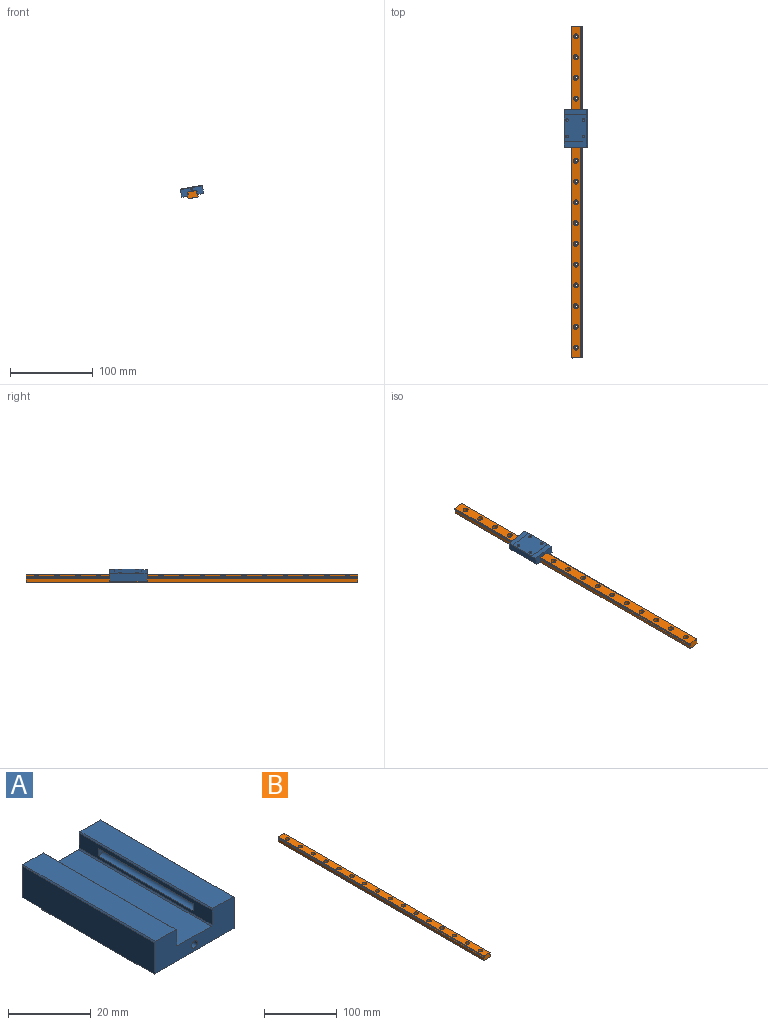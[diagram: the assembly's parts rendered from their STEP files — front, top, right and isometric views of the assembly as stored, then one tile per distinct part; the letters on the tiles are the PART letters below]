
ASSEMBLY  parts=2 mates=1
PART A: 37 faces, bbox 27x45.4x10 mm
  f0: plane 45.4x0.3mm, normal (-0.71,0,0.71), area 19.3mm2, adj f3,f6,f22,f23
  f1: plane 45.4x0.3mm, normal (0.71,0,0.71), area 19.3mm2, adj f10,f11,f22,f23
  f2: plane 45.4x0.3mm, normal (0.71,0,0.71), area 19.3mm2, adj f6,f7,f22,f23
  f3: plane 45.4x4.4mm, normal (-1,0,0), area 129.2mm2, adj f0,f5,f17,f20,f22,f23,f24
  f4: plane 45.4x11.4mm, normal (0,0,1), area 517.6mm2, adj f16,f17,f22,f23
  f5: cylinder r=1.15mm len=32.4mm, axis (0,-1,0), area 141.5mm2, adj f3,f20,f24
  f6: plane 45.4x6.9mm, normal (0,0,1), area 313.3mm2, adj f0,f2,f22,f23
  f7: plane 45.4x9.4mm, normal (1,0,0), area 424.2mm2, adj f2,f15,f18,f21,f22,f23,f25,f35
  f8: plane 32.4x26.4mm, normal (0,0,-1), area 821.1mm2, adj f14,f15,f18,f27,f29,f31,f33,f35
  f9: plane 45.4x9.4mm, normal (-1,0,0), area 424.2mm2, adj f14,f18,f21,f22,f23,f25,f34,f35
  f10: plane 45.4x6.9mm, normal (0,0,1), area 313.3mm2, adj f1,f22,f23,f34
  f11: plane 45.4x4.4mm, normal (1,0,0), area 129.2mm2, adj f1,f12,f16,f19,f22,f23,f36
  f12: cylinder r=1.15mm len=32.4mm, axis (0,-1,0), area 141.5mm2, adj f11,f19,f36
  f13: cylinder r=1mm len=45.4mm, axis (0,-1,0), area 285.3mm2, adj f22,f23
  f14: plane 32.4x0.3mm, normal (-0.71,0,-0.71), area 13.7mm2, adj f8,f9,f18,f35
  f15: plane 32.4x0.3mm, normal (0.71,0,-0.71), area 13.7mm2, adj f7,f8,f18,f35
  f16: plane 45.4x0.3mm, normal (0.71,0,0.71), area 19.3mm2, adj f4,f11,f22,f23
  f17: plane 45.4x0.3mm, normal (-0.71,0,0.71), area 19.3mm2, adj f3,f4,f22,f23
  f18: plane 27x0.5mm, normal (0,-1,0), area 13.4mm2, adj f7,f8,f9,f14,f15,f21
  f19: plane 2.3x1.52mm, normal (0,1,0), area 2.9mm2, adj f11,f12
  f20: plane 2.3x1.52mm, normal (0,1,0), area 2.9mm2, adj f3,f5
  f21: plane 27x6.5mm, normal (0,0,-1), area 175.5mm2, adj f7,f9,f18,f22
  f22: plane 27x9.5mm, normal (0,-1,0), area 193.3mm2, adj f0,f1,f2,f3,f4,f6,f7,f9
  f23: plane 27x9.5mm, normal (0,1,0), area 193.3mm2, adj f0,f1,f2,f3,f4,f6,f7,f9
  f24: plane 2.3x1.52mm, normal (0,-1,0), area 2.9mm2, adj f3,f5
  f25: plane 27x6.5mm, normal (0,0,-1), area 175.5mm2, adj f7,f9,f23,f35
  f26: cone r=857.17mm half-angle=59deg, axis (0,0,-1), area 10mm2, adj f27
  f27: cylinder r=1.65mm len=3.5mm, axis (0,0,1), area 36.3mm2, adj f8,f26
  f28: cone r=857.17mm half-angle=59deg, axis (0,0,-1), area 10mm2, adj f29
  f29: cylinder r=1.65mm len=3.5mm, axis (0,0,1), area 36.3mm2, adj f8,f28
  f30: cone r=857.17mm half-angle=59deg, axis (0,0,-1), area 10mm2, adj f31
  f31: cylinder r=1.65mm len=3.5mm, axis (0,0,1), area 36.3mm2, adj f8,f30
  f32: cone r=857.17mm half-angle=59deg, axis (0,0,-1), area 10mm2, adj f33
  f33: cylinder r=1.65mm len=3.5mm, axis (0,0,1), area 36.3mm2, adj f8,f32
  f34: plane 45.4x0.3mm, normal (-0.71,0,0.71), area 19.3mm2, adj f9,f10,f22,f23
  f35: plane 27x0.5mm, normal (0,1,0), area 13.4mm2, adj f7,f8,f9,f14,f15,f25
  f36: plane 2.3x1.52mm, normal (0,-1,0), area 2.9mm2, adj f11,f12
PART B: 70 faces, bbox 12x400x8 mm
  f0: plane 400x0.51mm, normal (0,0,1), area 203.9mm2, adj f1,f19,f20,f51
  f1: plane 400x0.3mm, normal (1,0,0), area 120mm2, adj f0,f2,f20,f51
  f2: plane 400x0.51mm, normal (0,0,-1), area 203.9mm2, adj f1,f3,f20,f51
  f3: cylinder r=1.15mm len=400mm, axis (0,1,0), area 511.7mm2, adj f2,f4,f20,f51
  f4: plane 400x0.86mm, normal (1,0,0), area 344.4mm2, adj f3,f5,f20,f51
  f5: plane 400x0.35mm, normal (0.71,0,0.71), area 198mm2, adj f4,f6,f20,f51
  f6: plane 400x11.3mm, normal (0,0,1), area 4067.6mm2, adj f5,f7,f20,f23,f26,f29,f32,f35
  f7: plane 400x0.35mm, normal (-0.71,0,0.71), area 198mm2, adj f6,f8,f20,f51
  f8: plane 400x0.86mm, normal (-1,0,0), area 344.4mm2, adj f7,f9,f20,f51
  f9: cylinder r=1.15mm len=400mm, axis (0,1,0), area 511.7mm2, adj f8,f10,f20,f51
  f10: plane 400x0.51mm, normal (0,0,-1), area 203.9mm2, adj f9,f11,f20,f51
  f11: plane 400x0.3mm, normal (-1,0,0), area 120mm2, adj f10,f12,f20,f51
  f12: plane 400x0.51mm, normal (0,0,1), area 203.9mm2, adj f11,f13,f20,f51
  f13: cylinder r=1.15mm len=400mm, axis (0,1,0), area 511.7mm2, adj f12,f14,f20,f51
  f14: plane 400x4.26mm, normal (-1,0,0), area 1704.5mm2, adj f13,f15,f20,f51
  f15: plane 400x0.35mm, normal (-0.71,0,-0.71), area 198mm2, adj f14,f16,f20,f51
  f16: plane 400x11.3mm, normal (0,0,-1), area 4366.1mm2, adj f15,f17,f20,f21,f24,f27,f30,f33
  f17: plane 400x0.35mm, normal (0.71,0,-0.71), area 198mm2, adj f16,f18,f20,f51
  f18: plane 400x4.26mm, normal (1,0,0), area 1704.5mm2, adj f17,f19,f20,f51
  f19: cylinder r=1.15mm len=400mm, axis (0,1,0), area 511.7mm2, adj f0,f18,f20,f51
  f20: plane 12x8mm, normal (0,-1,0), area 93mm2, adj f0,f1,f2,f3,f4,f5,f6,f7
  f21: cylinder r=1.75mm len=3.5mm, axis (0,0,1), area 38.5mm2, adj f16,f22
  f22: plane 6x6mm, normal (0,0,1), area 18.7mm2, adj f21,f23
  f23: cylinder r=3mm len=6mm, axis (0,0,1), area 84.8mm2, adj f6,f22
  f24: cylinder r=1.75mm len=3.5mm, axis (0,0,1), area 38.5mm2, adj f16,f25
  f25: plane 6x6mm, normal (0,0,1), area 18.7mm2, adj f24,f26
  f26: cylinder r=3mm len=6mm, axis (0,0,1), area 84.8mm2, adj f6,f25
  f27: cylinder r=1.75mm len=3.5mm, axis (0,0,1), area 38.5mm2, adj f16,f28
  f28: plane 6x6mm, normal (0,0,1), area 18.7mm2, adj f27,f29
  f29: cylinder r=3mm len=6mm, axis (0,0,1), area 84.8mm2, adj f6,f28
  f30: cylinder r=1.75mm len=3.5mm, axis (0,0,1), area 38.5mm2, adj f16,f31
  f31: plane 6x6mm, normal (0,0,1), area 18.7mm2, adj f30,f32
  f32: cylinder r=3mm len=6mm, axis (0,0,1), area 84.8mm2, adj f6,f31
  f33: cylinder r=1.75mm len=3.5mm, axis (0,0,1), area 38.5mm2, adj f16,f34
  f34: plane 6x6mm, normal (0,0,1), area 18.7mm2, adj f33,f35
  f35: cylinder r=3mm len=6mm, axis (0,0,1), area 84.8mm2, adj f6,f34
  f36: cylinder r=1.75mm len=3.5mm, axis (0,0,1), area 38.5mm2, adj f16,f37
  f37: plane 6x6mm, normal (0,0,1), area 18.7mm2, adj f36,f38
  f38: cylinder r=3mm len=6mm, axis (0,0,1), area 84.8mm2, adj f6,f37
  f39: cylinder r=1.75mm len=3.5mm, axis (0,0,1), area 38.5mm2, adj f16,f40
  f40: plane 6x6mm, normal (0,0,1), area 18.7mm2, adj f39,f41
  f41: cylinder r=3mm len=6mm, axis (0,0,1), area 84.8mm2, adj f6,f40
  f42: cylinder r=1.75mm len=3.5mm, axis (0,0,1), area 38.5mm2, adj f16,f43
  f43: plane 6x6mm, normal (0,0,1), area 18.7mm2, adj f42,f44
  f44: cylinder r=3mm len=6mm, axis (0,0,1), area 84.8mm2, adj f6,f43
  f45: cylinder r=1.75mm len=3.5mm, axis (0,0,1), area 38.5mm2, adj f16,f46
  f46: plane 6x6mm, normal (0,0,1), area 18.7mm2, adj f45,f47
  f47: cylinder r=3mm len=6mm, axis (0,0,1), area 84.8mm2, adj f6,f46
  f48: cylinder r=1.75mm len=3.5mm, axis (0,0,1), area 38.5mm2, adj f16,f49
  f49: plane 6x6mm, normal (0,0,1), area 18.7mm2, adj f48,f50
  f50: cylinder r=3mm len=6mm, axis (0,0,1), area 84.8mm2, adj f6,f49
  f51: plane 12x8mm, normal (0,1,0), area 93mm2, adj f0,f1,f2,f3,f4,f5,f6,f7
  f52: cylinder r=1.75mm len=3.5mm, axis (0,0,1), area 38.5mm2, adj f16,f53
  f53: plane 6x6mm, normal (0,0,1), area 18.7mm2, adj f52,f54
  f54: cylinder r=3mm len=6mm, axis (0,0,1), area 84.8mm2, adj f6,f53
  f55: cylinder r=1.75mm len=3.5mm, axis (0,0,1), area 38.5mm2, adj f16,f56
  f56: plane 6x6mm, normal (0,0,1), area 18.7mm2, adj f55,f57
  f57: cylinder r=3mm len=6mm, axis (0,0,1), area 84.8mm2, adj f6,f56
  f58: cylinder r=1.75mm len=3.5mm, axis (0,0,1), area 38.5mm2, adj f16,f59
  f59: plane 6x6mm, normal (0,0,1), area 18.7mm2, adj f58,f60
  f60: cylinder r=3mm len=6mm, axis (0,0,1), area 84.8mm2, adj f6,f59
  f61: cylinder r=1.75mm len=3.5mm, axis (0,0,1), area 38.5mm2, adj f16,f62
  f62: plane 6x6mm, normal (0,0,1), area 18.7mm2, adj f61,f63
  f63: cylinder r=3mm len=6mm, axis (0,0,1), area 84.8mm2, adj f6,f62
  f64: cylinder r=1.75mm len=3.5mm, axis (0,0,1), area 38.5mm2, adj f16,f65
  f65: plane 6x6mm, normal (0,0,1), area 18.7mm2, adj f64,f66
  f66: cylinder r=3mm len=6mm, axis (0,0,1), area 84.8mm2, adj f6,f65
  f67: cylinder r=1.75mm len=3.5mm, axis (0,0,1), area 38.5mm2, adj f16,f68
  f68: plane 6x6mm, normal (0,0,1), area 18.7mm2, adj f67,f69
  f69: cylinder r=3mm len=6mm, axis (0,0,1), area 84.8mm2, adj f6,f68
PLACE A rot(axis=(0,1,0),170deg) t=(-31.25,170.03,86.89)mm
PLACE B rot(axis=(0,-1,0),10deg) t=(-31.25,-97.87,86.89)mm
MATE slider B.f20 <-> A.f22  axis (0,-1,0) through (-31.25,-122.87,86.89)mm
